# Revit family: SoapDispenserHolder-Vitra-OriginSeries-A44892
name_source: partatom
category: Plumbing Fixtures
revit_build: Autodesk Revit 2017 (Build: 20160225_1515(x64)
units: mm (PartAtom-declared; Revit-internal decimal feet)

## family parameters
Cut with Voids When Loaded = No
Host = Face
OmniClass Number = 23.45.05.14.99
OmniClass Title = Other Sanitary Washing Plumbing Fixtures
Part Type = Normal
Room Calculation Point = No
Round Connector Dimension = Use Diameter
Shared = Yes

## types (4) — shared parameters
BIMobject category = Sanitary - Accessories
CW Connection = No
Depth(mm) = 96 mm  [stored 0.314961 ft]
Description = Origin Liquid Soap Dispenser Holder
Design country = Turkey
HW Connection = No
Height(mm) = 134 mm
IFC Classification = Sanitary Terminal
Manufacturer = Vitra
Manufacturer name = Vitra
Masterformat 2014 Code = 01 52 19
Masterformat 2014 Description = Sanitary Facilities
MountingType = Wall-mounted
NBS Referans Code = 31-75
NBS Referans Description = Sanitary Accessories
Nominal height = 0.000
Nominal width = 0.000
OmniClass Code = 23-21 43 15 23
OmniClass Description = Lotion Dispensers
Product Type = Built-in Liquid Soap Dispenser Holder
Product certification = https://vitraglobal.com
Product data url = https://www.vitraglobal.com
Product family = OriginSeries
Product group = Liquid Soap Dispenser Holder
UNSPSC Code = 301815
UNSPSC Description = Sanitary ware
URL = https://vitraglobal.com
Uniclass 1.4 Code = L8244
Uniclass 1.4 Description = Sanitary dispensers
Uniclass 2.0 Code = PR-31-75
Uniclass 2.0 Description = Sanitary Accessories
Uniclass 2015 Code = Pr_40_70_22
Uniclass 2015 Name = Dispensers and acceptance units
Uniformat II Description = FURNISHINGS
Vent Connection = No
Warranty Period (Year) = 5 years
Waste Connection = No
Weight Net (kg) = 0,350
Width(mm) = 80 mm  [stored 0.262467 ft]
Youtube = https://www.youtube.com
zero-valued in all types: CWFU, Cost, Default Elevation, HWFU, WFU

## per-type parameters (varying)
| type | Article No. (default) | Coating Material | Color | Model | Product SKU |
| LiquidSoapDispenserHolder-Vitra-OriginSeries(Chrome)-A44892 | A44892 | Vitra-Chrome | Chrome | A44892 | A44892 |
| LiquidSoapDispenserHolder-Vitra-OriginSeries(Copper)-A4489226 | A4489226 | Vitra-Copper | Copper | A4489226 | A4489226 |
| LiquidSoapDispenserHolder-Vitra-OriginSeries(BrushedNickel)-A4489234 | A4489234 | Vitra-Brushed Nickel | Brushed Nickel | A4489234 | A4489234 |
| LiquidSoapDispenserHolder-Vitra-OriginSeries(Black)-A4489236 | A4489236 | Vitra-Black | Black | A4489236 | A4489236 |

note: [stored X ft] marks values corroborated as IEEE doubles in the binary element streams (Revit-internal decimal feet)

## geometry (parser evidence)
native form markers: Sweep x3
no freeform markers — native parametric forms only
